# Revit family: Bath-Drop_In-KOHLER-Greek-K-1490_1
name_source: partatom
category: Plumbing Fixtures
units: mm (PartAtom-declared; Revit-internal decimal feet)

## family parameters
Cut with Voids When Loaded = No
Host = Face
OmniClass Number = 23.31.15.00
OmniClass Title = Bathtubs
Part Type = Normal
Room Calculation Point = No
Round Connector Dimension = Use Diameter
Shared = No

## types (2) — shared parameters
ADA Compliant = No
Assembly Code = D2010500
CW Connection = No
Cold Water Inlet = Cold Water Inlet
Date Modified = 02/23/2023
Default Elevation = 0"
Description = 48 Inch X 32 Inch Drop In Bath
Drain Included = No
Flow Rate = 0 GPM
HW Connection = No
Height = 24 9/16"
Hot Water Inlet = Hot Water Inlet
Length = 47 11/16"
Manufacturer = Kohler Co.
Master Format 2014 = 22 41 19
Master Format 2014 Name = Residential Bathtubs
Material = Acrylic
Pressure = 0.00 psi
Product Documentation Link = https://www.us.kohler.com
Product Name = Greek
Product Page URL = http://www.us.kohler.com
URL = https://www.us.kohler.com
Vent Connection = No
Waste Connection = Yes
Waste Water Outlet = Waste Water Outlet
WaterSense Certified = No
Width = 29 9/16"

## per-type parameters (varying)
| type | Finish | Model | Type |
| 0-White | KOHLER-Acrylic-0-White | K-1490-X-0 | 1 |
| G9-Sandbar | KOHLER-Acrylic-G9-Sandbar | K-1490-X-G9 | 2 |

## geometry (parser evidence)
native form markers: Sweep x5
no freeform markers — native parametric forms only
